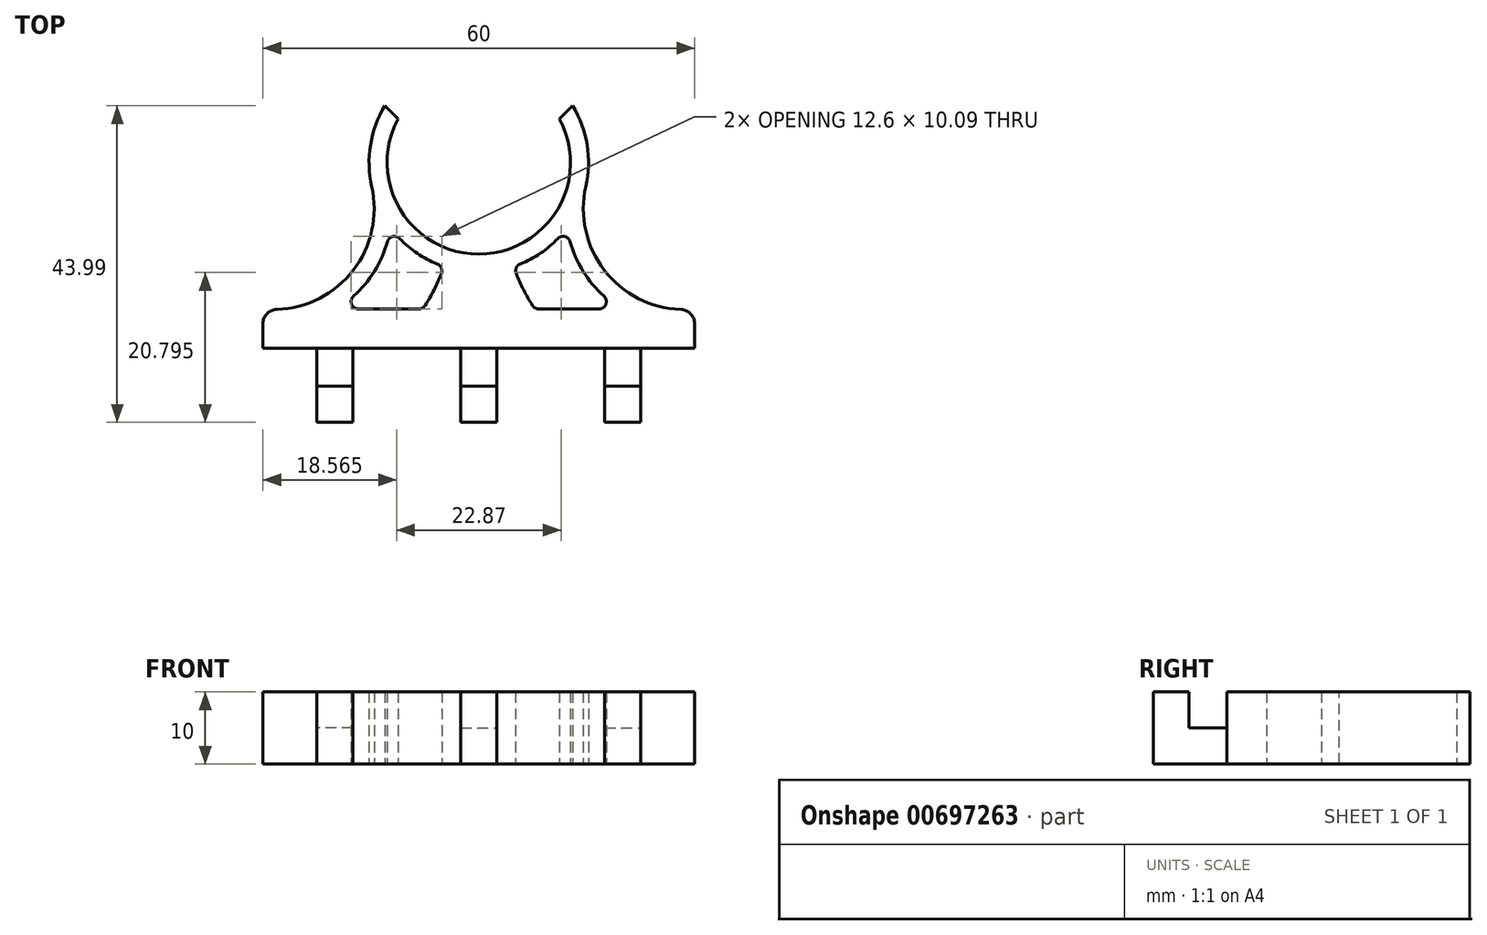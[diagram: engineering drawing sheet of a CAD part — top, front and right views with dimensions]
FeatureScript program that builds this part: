
annotation { "Feature Type Name" : "Feature", "Feature Type Description" : "" }
export const myFeature = defineFeature(function(context is Context, id is Id, definition is map)
    precondition{}
    {
        {
            var Q0;
            Q0=qCreatedBy(makeId("Top.planeOp"),FACE);
            var sketch = newSketch(context, id + "F0", { "sketchPlane" : qUnion([Q0])});
            skCircle(sketch, "E0", {"center": v(0, 0) * mm, "radius": 12.5 * mm});
            skCircle(sketch, "E1", {"center": v(0, 0) * mm, "radius": 12.75 * mm});
            skCircle(sketch, "E2", {"center": v(0, 0) * mm, "radius": 15.25 * mm});
            skLineSegment(sketch, "E3", {"start": v(-9.58, 8.03) * mm, "end": v(-9.77, 8.2) * mm});
            skLineSegment(sketch, "E4", {"start": v(0, -15.25) * mm, "end": v(0, -25.35) * mm});
            skLineSegment(sketch, "E5", {"start": v(0, -25.35) * mm, "end": v(30, -25.35) * mm});
            skLineSegment(sketch, "E6.MirrorCS", {"start": v(0, -25.35) * mm, "end": v(-30, -25.35) * mm});
            skLineSegment(sketch, "E7", {"start": v(-30, -25.35) * mm, "end": v(-30, -20.35) * mm});
            skLineSegment(sketch, "E8.MirrorCS", {"start": v(30, -25.35) * mm, "end": v(30, -20.35) * mm});
            skCircle(sketch, "E9", {"center": v(-28.54, -6.43) * mm, "radius": 14 * mm});
            skCircle(sketch, "E10", {"center": v(-28.54, -6.43) * mm, "radius": 25 * mm});
            skLineSegment(sketch, "E11", {"start": v(-30, -20.35) * mm, "end": v(30, -20.35) * mm});
            skCircle(sketch, "E12.MirrorC", {"center": v(28.54, -6.43) * mm, "radius": 14 * mm});
            skCircle(sketch, "E13.MirrorC", {"center": v(28.54, -6.43) * mm, "radius": 25 * mm});
            skCircle(sketch, "E14", {"center": v(-28.54, -6.43) * mm, "radius": 16.5 * mm});
            skCircle(sketch, "E15.MirrorC", {"center": v(28.54, -6.43) * mm, "radius": 16.5 * mm});
            skLineSegment(sketch, "E16", {"start": v(0, -5.17) * mm, "end": v(16.49, 11.32) * mm});
            skLineSegment(sketch, "E17.MirrorCS", {"start": v(0, -5.17) * mm, "end": v(-16.49, 11.32) * mm});
            skPoint(sketch, "E18.trimOffspring.end.orphan", {"position": v(-16.49, 11.32) * mm});
            skLineSegment(sketch, "E19", {"start": v(-30, -25.35) * mm, "end": v(-30, -25.85) * mm});
            skLineSegment(sketch, "E20", {"start": v(30, -25.35) * mm, "end": v(30, -25.85) * mm});
            skLineSegment(sketch, "E21", {"start": v(-30, -25.85) * mm, "end": v(30, -25.85) * mm});
            skSolve(sketch);
        }
        {
            var Q0;
            {var subQ2=sQuery(id+"F0.wireOp",EDGE,"E10");var subQ4=sQuery(id+"F0.wireOp",EDGE,"E1");var subQ5=makeQuery(id+"F0.imprint","INTERSECT",VERTEX,{"disambiguationData":[OD(1.0)],"derivedFrom":[subQ4,subQ2]});Q0=makeQuery(id+"F0.imprint","IMPRINT",FACE,{"disambiguationData":[TD([[makeQuery(id+"F0.imprint","IMPRINT",EDGE,{"disambiguationData":[TD([[subQ5,-1.0]])],"derivedFrom":subQ4}),-1.0]])]});}
            var Q1;
            {var subQ0=sQuery(id+"F0.wireOp",EDGE,"E4");var subQ1=sQuery(id+"F0.wireOp",EDGE,"E2");var subQ2=makeQuery(id+"F0.imprint","INTERSECT",VERTEX,{"derivedFrom":[subQ1,subQ0]});Q1=makeQuery(id+"F0.imprint","IMPRINT",FACE,{"disambiguationData":[TD([[makeQuery(id+"F0.imprint","IMPRINT",EDGE,{"disambiguationData":[TD([[subQ2,1.0]])],"derivedFrom":subQ1}),-1.0]])]});}
            var Q2;
            {var subQ0=sQuery(id+"F0.wireOp",EDGE,"E4");var subQ1=sQuery(id+"F0.wireOp",EDGE,"E2");var subQ2=makeQuery(id+"F0.imprint","INTERSECT",VERTEX,{"derivedFrom":[subQ1,subQ0]});Q2=makeQuery(id+"F0.imprint","IMPRINT",FACE,{"disambiguationData":[TD([[makeQuery(id+"F0.imprint","IMPRINT",EDGE,{"disambiguationData":[TD([[subQ2,-1.0]])],"derivedFrom":subQ1}),-1.0]])]});}
            var Q3;
            {var subQ6=sQuery(id+"F0.wireOp",EDGE,"E7");Q3=makeQuery(id+"F0.imprint","IMPRINT",FACE,{"disambiguationData":[TD([[makeQuery(id+"F0.imprint","IMPRINT",EDGE,{"derivedFrom":subQ6}),-1.0]])]});}
            var Q4;
            {var subQ0=sQuery(id+"F0.wireOp",EDGE,"E6.MirrorCS");var subQ5=sQuery(id+"F0.wireOp",EDGE,"E10");var subQ7=makeQuery(id+"F0.imprint","INTERSECT",VERTEX,{"derivedFrom":[subQ0,subQ5]});Q4=makeQuery(id+"F0.imprint","IMPRINT",FACE,{"disambiguationData":[TD([[makeQuery(id+"F0.imprint","IMPRINT",EDGE,{"disambiguationData":[TD([[subQ7,-1.0]])],"derivedFrom":subQ5}),-1.0]])]});}
            var Q5;
            {var subQ1=sQuery(id+"F0.wireOp",EDGE,"E4");var subQ3=sQuery(id+"F0.wireOp",EDGE,"E11");var subQ4=makeQuery(id+"F0.imprint","INTERSECT",VERTEX,{"derivedFrom":[subQ1,subQ3]});Q5=makeQuery(id+"F0.imprint","IMPRINT",FACE,{"disambiguationData":[TD([[makeQuery(id+"F0.imprint","IMPRINT",EDGE,{"disambiguationData":[TD([[subQ4,-1.0]])],"derivedFrom":subQ3}),-1.0]])]});}
            var Q6;
            {var subQ2=sQuery(id+"F0.wireOp",EDGE,"E8.MirrorCS");Q6=makeQuery(id+"F0.imprint","IMPRINT",FACE,{"disambiguationData":[TD([[makeQuery(id+"F0.imprint","IMPRINT",EDGE,{"derivedFrom":subQ2}),1.0]])]});}
            var Q7;
            {var subQ0=sQuery(id+"F0.wireOp",EDGE,"E14");var subQ1=sQuery(id+"F0.wireOp",EDGE,"E2");var subQ2=makeQuery(id+"F0.imprint","INTERSECT",VERTEX,{"disambiguationData":[OD(0.0)],"derivedFrom":[subQ1,subQ0]});Q7=makeQuery(id+"F0.imprint","IMPRINT",FACE,{"disambiguationData":[TD([[makeQuery(id+"F0.imprint","IMPRINT",EDGE,{"disambiguationData":[TD([[subQ2,-1.0]])],"derivedFrom":subQ1}),1.0]])]});}
            var Q8;
            {var subQ0=sQuery(id+"F0.wireOp",EDGE,"E14");var subQ1=sQuery(id+"F0.wireOp",EDGE,"E1");var subQ2=makeQuery(id+"F0.imprint","INTERSECT",VERTEX,{"derivedFrom":[subQ1,subQ0]});Q8=makeQuery(id+"F0.imprint","IMPRINT",FACE,{"disambiguationData":[TD([[makeQuery(id+"F0.imprint","IMPRINT",EDGE,{"disambiguationData":[TD([[subQ2,-1.0]])],"derivedFrom":subQ1}),-1.0]])]});}
            var Q9;
            {var subQ0=sQuery(id+"F0.wireOp",EDGE,"E13.MirrorC");var subQ1=sQuery(id+"F0.wireOp",EDGE,"E1");var subQ2=makeQuery(id+"F0.imprint","INTERSECT",VERTEX,{"disambiguationData":[OD(1.0)],"derivedFrom":[subQ1,subQ0]});Q9=makeQuery(id+"F0.imprint","IMPRINT",FACE,{"disambiguationData":[TD([[makeQuery(id+"F0.imprint","IMPRINT",EDGE,{"disambiguationData":[TD([[subQ2,-1.0]])],"derivedFrom":subQ1}),-1.0]])]});}
            var Q10;
            {var subQ0=sQuery(id+"F0.wireOp",EDGE,"E15.MirrorC");var subQ1=sQuery(id+"F0.wireOp",EDGE,"E2");var subQ2=makeQuery(id+"F0.imprint","INTERSECT",VERTEX,{"disambiguationData":[OD(1.0)],"derivedFrom":[subQ1,subQ0]});Q10=makeQuery(id+"F0.imprint","IMPRINT",FACE,{"disambiguationData":[TD([[makeQuery(id+"F0.imprint","IMPRINT",EDGE,{"disambiguationData":[TD([[subQ2,-1.0]])],"derivedFrom":subQ1}),1.0]])]});}
            var Q11;
            {var subQ0=sQuery(id+"F0.wireOp",EDGE,"E9");var subQ1=sQuery(id+"F0.wireOp",EDGE,"E2");var subQ2=makeQuery(id+"F0.imprint","INTERSECT",VERTEX,{"derivedFrom":[subQ1,subQ0]});Q11=makeQuery(id+"F0.imprint","IMPRINT",FACE,{"disambiguationData":[TD([[makeQuery(id+"F0.imprint","IMPRINT",EDGE,{"disambiguationData":[TD([[subQ2,-1.0]])],"derivedFrom":subQ1}),-1.0]])]});}
            var Q12;
            {var subQ5=sQuery(id+"F0.wireOp",EDGE,"E6.MirrorCS");var subQ7=sQuery(id+"F0.wireOp",EDGE,"E7");var subQ8=makeQuery(id+"F0.imprint","INTERSECT",VERTEX,{"derivedFrom":[subQ5,subQ7]});Q12=makeQuery(id+"F0.imprint","IMPRINT",FACE,{"disambiguationData":[TD([[makeQuery(id+"F0.imprint","IMPRINT",EDGE,{"disambiguationData":[TD([[subQ8,1.0]])],"derivedFrom":subQ5}),-1.0]])]});}
            var Q13;
            {var subQ0=sQuery(id+"F0.wireOp",EDGE,"E15.MirrorC");var subQ1=sQuery(id+"F0.wireOp",EDGE,"E2");var subQ2=makeQuery(id+"F0.imprint","INTERSECT",VERTEX,{"disambiguationData":[OD(1.0)],"derivedFrom":[subQ1,subQ0]});Q13=makeQuery(id+"F0.imprint","IMPRINT",FACE,{"disambiguationData":[TD([[makeQuery(id+"F0.imprint","IMPRINT",EDGE,{"disambiguationData":[TD([[subQ2,-1.0]])],"derivedFrom":subQ1}),-1.0]])]});}
            var Q14;
            {var subQ1=sQuery(id+"F0.wireOp",EDGE,"E5");var subQ7=sQuery(id+"F0.wireOp",EDGE,"E8.MirrorCS");var subQ8=makeQuery(id+"F0.imprint","INTERSECT",VERTEX,{"derivedFrom":[subQ1,subQ7]});Q14=makeQuery(id+"F0.imprint","IMPRINT",FACE,{"disambiguationData":[TD([[makeQuery(id+"F0.imprint","IMPRINT",EDGE,{"disambiguationData":[TD([[subQ8,1.0]])],"derivedFrom":subQ1}),1.0]])]});}
            var Q15;
            {var subQ0=sQuery(id+"F0.wireOp",EDGE,"E17.MirrorCS");var subQ1=sQuery(id+"F0.wireOp",EDGE,"E1");var subQ2=makeQuery(id+"F0.imprint","INTERSECT",VERTEX,{"derivedFrom":[subQ1,subQ0]});Q15=makeQuery(id+"F0.imprint","IMPRINT",FACE,{"disambiguationData":[TD([[makeQuery(id+"F0.imprint","IMPRINT",EDGE,{"disambiguationData":[TD([[subQ2,-1.0]])],"derivedFrom":subQ1}),-1.0]])]});}
            var Q16;
            {var subQ0=sQuery(id+"F0.wireOp",EDGE,"E16");var subQ1=sQuery(id+"F0.wireOp",EDGE,"E1");var subQ2=makeQuery(id+"F0.imprint","INTERSECT",VERTEX,{"derivedFrom":[subQ1,subQ0]});Q16=makeQuery(id+"F0.imprint","IMPRINT",FACE,{"disambiguationData":[TD([[makeQuery(id+"F0.imprint","IMPRINT",EDGE,{"disambiguationData":[TD([[subQ2,1.0]])],"derivedFrom":subQ1}),-1.0]])]});}
            var Q17;
            {var subQ0=sQuery(id+"F0.wireOp",EDGE,"E19");Q17=makeQuery(id+"F0.imprint","IMPRINT",FACE,{"disambiguationData":[TD([[makeQuery(id+"F0.imprint","IMPRINT",EDGE,{"derivedFrom":subQ0}),1.0]])]});}
            var Q18;
            {var subQ0=sQuery(id+"F0.wireOp",EDGE,"E21");var subQ7=sQuery(id+"F0.wireOp",EDGE,"E10");var subQ9=makeQuery(id+"F0.imprint","INTERSECT",VERTEX,{"derivedFrom":[subQ7,subQ0]});Q18=makeQuery(id+"F0.imprint","IMPRINT",FACE,{"disambiguationData":[TD([[makeQuery(id+"F0.imprint","IMPRINT",EDGE,{"disambiguationData":[TD([[subQ9,-1.0]])],"derivedFrom":subQ7}),-1.0]])]});}
            var Q19;
            {var subQ0=sQuery(id+"F0.wireOp",EDGE,"E20");Q19=makeQuery(id+"F0.imprint","IMPRINT",FACE,{"disambiguationData":[TD([[makeQuery(id+"F0.imprint","IMPRINT",EDGE,{"derivedFrom":subQ0}),-1.0]])]});}
            extrude(context, id + "F1", {"entities" : qUnion([Q0, Q1, Q2, Q3, Q4, Q5, Q6, Q7, Q8, Q9, Q10, Q11, Q12, Q13, Q14, Q15, Q16, Q17, Q18, Q19]), "depth" : 10 * mm, "offsetDistance" : 25 * mm});
        }
        {
            var Q0;
            Q0=makeQuery(id+"F1.opExtrude","SWEPT_EDGE",EDGE,{"disambiguationData":[OSD([sQuery(id+"F0.wireOp",EDGE,"E10"),sQuery(id+"F0.wireOp",EDGE,"E11")])]});
            var Q1;
            Q1=makeQuery(id+"F1.opExtrude","SWEPT_EDGE",EDGE,{"disambiguationData":[OSD([sQuery(id+"F0.wireOp",EDGE,"E2"),sQuery(id+"F0.wireOp",EDGE,"E10")])]});
            var Q2;
            Q2=makeQuery(id+"F1.opExtrude","SWEPT_EDGE",EDGE,{"disambiguationData":[OSD([sQuery(id+"F0.wireOp",EDGE,"E2"),sQuery(id+"F0.wireOp",EDGE,"E14")])]});
            var Q3;
            Q3=makeQuery(id+"F1.opExtrude","SWEPT_EDGE",EDGE,{"disambiguationData":[OSD([sQuery(id+"F0.wireOp",EDGE,"E11"),sQuery(id+"F0.wireOp",EDGE,"E14")])]});
            var Q4;
            Q4=makeQuery(id+"F1.opExtrude","SWEPT_EDGE",EDGE,{"disambiguationData":[OSD([sQuery(id+"F0.wireOp",EDGE,"E11"),sQuery(id+"F0.wireOp",EDGE,"E13.MirrorC")])]});
            var Q5;
            Q5=makeQuery(id+"F1.opExtrude","SWEPT_EDGE",EDGE,{"disambiguationData":[OSD([sQuery(id+"F0.wireOp",EDGE,"E2"),sQuery(id+"F0.wireOp",EDGE,"E13.MirrorC")])]});
            var Q6;
            Q6=makeQuery(id+"F1.opExtrude","SWEPT_EDGE",EDGE,{"disambiguationData":[OSD([sQuery(id+"F0.wireOp",EDGE,"E2"),sQuery(id+"F0.wireOp",EDGE,"E15.MirrorC")])]});
            var Q7;
            Q7=makeQuery(id+"F1.opExtrude","SWEPT_EDGE",EDGE,{"disambiguationData":[OSD([sQuery(id+"F0.wireOp",EDGE,"E11"),sQuery(id+"F0.wireOp",EDGE,"E15.MirrorC")])]});
            fillet(context, id + "F2", {"entities" : qUnion([Q0, Q1, Q2, Q3, Q4, Q5, Q6, Q7]), "radius" : 1 * mm, "tangentPropagation" : true, "allowEdgeOverflow" : false});
        }
        {
            var Q0;
            Q0=makeQuery(id+"F1.opExtrude","SWEPT_EDGE",EDGE,{"disambiguationData":[OSD([sQuery(id+"F0.wireOp",EDGE,"E8.MirrorCS"),sQuery(id+"F0.wireOp",EDGE,"E11"),sQuery(id+"F0.wireOp",EDGE,"E12.MirrorC")])]});
            var Q1;
            Q1=makeQuery(id+"F1.opExtrude","SWEPT_EDGE",EDGE,{"disambiguationData":[OSD([sQuery(id+"F0.wireOp",EDGE,"E7"),sQuery(id+"F0.wireOp",EDGE,"E9"),sQuery(id+"F0.wireOp",EDGE,"E11")])]});
            fillet(context, id + "F3", {"entities" : qUnion([Q0, Q1]), "radius" : 2 * mm, "tangentPropagation" : true, "allowEdgeOverflow" : false});
        }
        {
            var Q0;
            Q0=makeQuery(id+"F1.opExtrude","SWEPT_FACE",FACE,{"disambiguationData":[OSD([sQuery(id+"F0.wireOp",EDGE,"E21")])]});
            var sketch = newSketch(context, id + "F4", { "sketchPlane" : qUnion([Q0])});
            skLineSegment(sketch, "E22.bottom", {"start": v(-2.5, 0) * mm, "end": v(2.5, 0) * mm});
            skLineSegment(sketch, "E22.top", {"start": v(-2.5, 5) * mm, "end": v(2.5, 5) * mm});
            skLineSegment(sketch, "E22.left", {"start": v(-2.5, 0) * mm, "end": v(-2.5, 5) * mm});
            skLineSegment(sketch, "E22.right", {"start": v(2.5, 0) * mm, "end": v(2.5, 5) * mm});
            skLineSegment(sketch, "E23.MirrorCS", {"start": v(-17.5, 5) * mm, "end": v(-22.5, 5) * mm});
            skLineSegment(sketch, "E24.MirrorCS", {"start": v(-17.5, 0) * mm, "end": v(-17.5, 5) * mm});
            skLineSegment(sketch, "E25.MirrorCS", {"start": v(-17.5, 0) * mm, "end": v(-22.5, 0) * mm});
            skLineSegment(sketch, "E26.MirrorCS", {"start": v(-22.5, 0) * mm, "end": v(-22.5, 5) * mm});
            skLineSegment(sketch, "E27.MirrorCS", {"start": v(17.5, 5) * mm, "end": v(22.5, 5) * mm});
            skLineSegment(sketch, "E28.MirrorCS", {"start": v(22.5, 0) * mm, "end": v(22.5, 5) * mm});
            skLineSegment(sketch, "E29.MirrorCS", {"start": v(17.5, 0) * mm, "end": v(22.5, 0) * mm});
            skLineSegment(sketch, "E30.MirrorCS", {"start": v(17.5, 0) * mm, "end": v(17.5, 5) * mm});
            skSolve(sketch);
        }
        {
            var Q0;
            Q0=makeQuery(id+"F4.imprint","IMPRINT",FACE,{"disambiguationData":[TD([[makeQuery(id+"F4.imprint","IMPRINT",EDGE,{"derivedFrom":sQuery(id+"F4.wireOp",EDGE,"E23.MirrorCS")}),1.0]])]});
            var Q1;
            Q1=makeQuery(id+"F4.imprint","IMPRINT",FACE,{"disambiguationData":[TD([[makeQuery(id+"F4.imprint","IMPRINT",EDGE,{"derivedFrom":sQuery(id+"F4.wireOp",EDGE,"E22.bottom")}),-1.0]])]});
            var Q2;
            Q2=makeQuery(id+"F4.imprint","IMPRINT",FACE,{"disambiguationData":[TD([[makeQuery(id+"F4.imprint","IMPRINT",EDGE,{"derivedFrom":sQuery(id+"F4.wireOp",EDGE,"E27.MirrorCS")}),-1.0]])]});
            var Q3;
            Q3=makeQuery(id+"F4.imprint","IMPRINT",FACE,{"disambiguationData":[TD([[makeQuery(id+"F4.imprint","IMPRINT",EDGE,{"derivedFrom":sQuery(id+"F4.wireOp",EDGE,"E22.bottom")}),1.0]])]});
            extrude(context, id + "F5", {"entities" : qUnion([Q0, Q1, Q2, Q3]), "operationType" : NewBodyOperationType.ADD, "depth" : 10.25 * mm, "offsetDistance" : 25 * mm});
        }
        {
            var Q0;
            Q0=makeQuery(id+"F5.opExtrude","SWEPT_FACE",FACE,{"disambiguationData":[OSD([sQuery(id+"F4.wireOp",EDGE,"E23.MirrorCS")])]});
            var sketch = newSketch(context, id + "F6", { "sketchPlane" : qUnion([Q0])});
            skLineSegment(sketch, "E31.bottom", {"start": v(-22.5, -36.1) * mm, "end": v(-17.5, -36.1) * mm});
            skLineSegment(sketch, "E31.top", {"start": v(-22.5, -31.1) * mm, "end": v(-17.5, -31.1) * mm});
            skLineSegment(sketch, "E31.left", {"start": v(-22.5, -36.1) * mm, "end": v(-22.5, -31.1) * mm});
            skLineSegment(sketch, "E31.right", {"start": v(-17.5, -36.1) * mm, "end": v(-17.5, -31.1) * mm});
            skSolve(sketch);
        }
        {
            var Q0;
            Q0=makeQuery(id+"F5.opExtrude","SWEPT_FACE",FACE,{"disambiguationData":[OSD([sQuery(id+"F4.wireOp",EDGE,"E22.top")])]});
            var sketch = newSketch(context, id + "F7", { "sketchPlane" : qUnion([Q0])});
            skLineSegment(sketch, "E32.bottom", {"start": v(-2.5, -36.1) * mm, "end": v(2.5, -36.1) * mm});
            skLineSegment(sketch, "E32.top", {"start": v(-2.5, -31.1) * mm, "end": v(2.5, -31.1) * mm});
            skLineSegment(sketch, "E32.left", {"start": v(-2.5, -36.1) * mm, "end": v(-2.5, -31.1) * mm});
            skLineSegment(sketch, "E32.right", {"start": v(2.5, -36.1) * mm, "end": v(2.5, -31.1) * mm});
            skSolve(sketch);
        }
        {
            var Q0;
            Q0=makeQuery(id+"F5.opExtrude","SWEPT_FACE",FACE,{"disambiguationData":[OSD([sQuery(id+"F4.wireOp",EDGE,"E27.MirrorCS")])]});
            var sketch = newSketch(context, id + "F8", { "sketchPlane" : qUnion([Q0])});
            skLineSegment(sketch, "E33.bottom", {"start": v(17.5, -36.1) * mm, "end": v(22.5, -36.1) * mm});
            skLineSegment(sketch, "E33.top", {"start": v(17.5, -31.1) * mm, "end": v(22.5, -31.1) * mm});
            skLineSegment(sketch, "E33.left", {"start": v(17.5, -36.1) * mm, "end": v(17.5, -31.1) * mm});
            skLineSegment(sketch, "E33.right", {"start": v(22.5, -36.1) * mm, "end": v(22.5, -31.1) * mm});
            skSolve(sketch);
        }
        {
            var Q0;
            Q0=makeQuery(id+"F6.imprint","IMPRINT",FACE,{"disambiguationData":[TD([[makeQuery(id+"F6.imprint","IMPRINT",EDGE,{"derivedFrom":sQuery(id+"F6.wireOp",EDGE,"E31.bottom")}),-1.0]])]});
            var Q1;
            Q1=makeQuery(id+"F7.imprint","IMPRINT",FACE,{"disambiguationData":[TD([[makeQuery(id+"F7.imprint","IMPRINT",EDGE,{"derivedFrom":sQuery(id+"F7.wireOp",EDGE,"E32.bottom")}),1.0]])]});
            var Q2;
            Q2=makeQuery(id+"F8.imprint","IMPRINT",FACE,{"disambiguationData":[TD([[makeQuery(id+"F8.imprint","IMPRINT",EDGE,{"derivedFrom":sQuery(id+"F8.wireOp",EDGE,"E33.bottom")}),1.0]])]});
            extrude(context, id + "F9", {"entities" : qUnion([Q0, Q1, Q2]), "operationType" : NewBodyOperationType.ADD, "depth" : 5 * mm, "offsetDistance" : 25 * mm});
        }
    });
